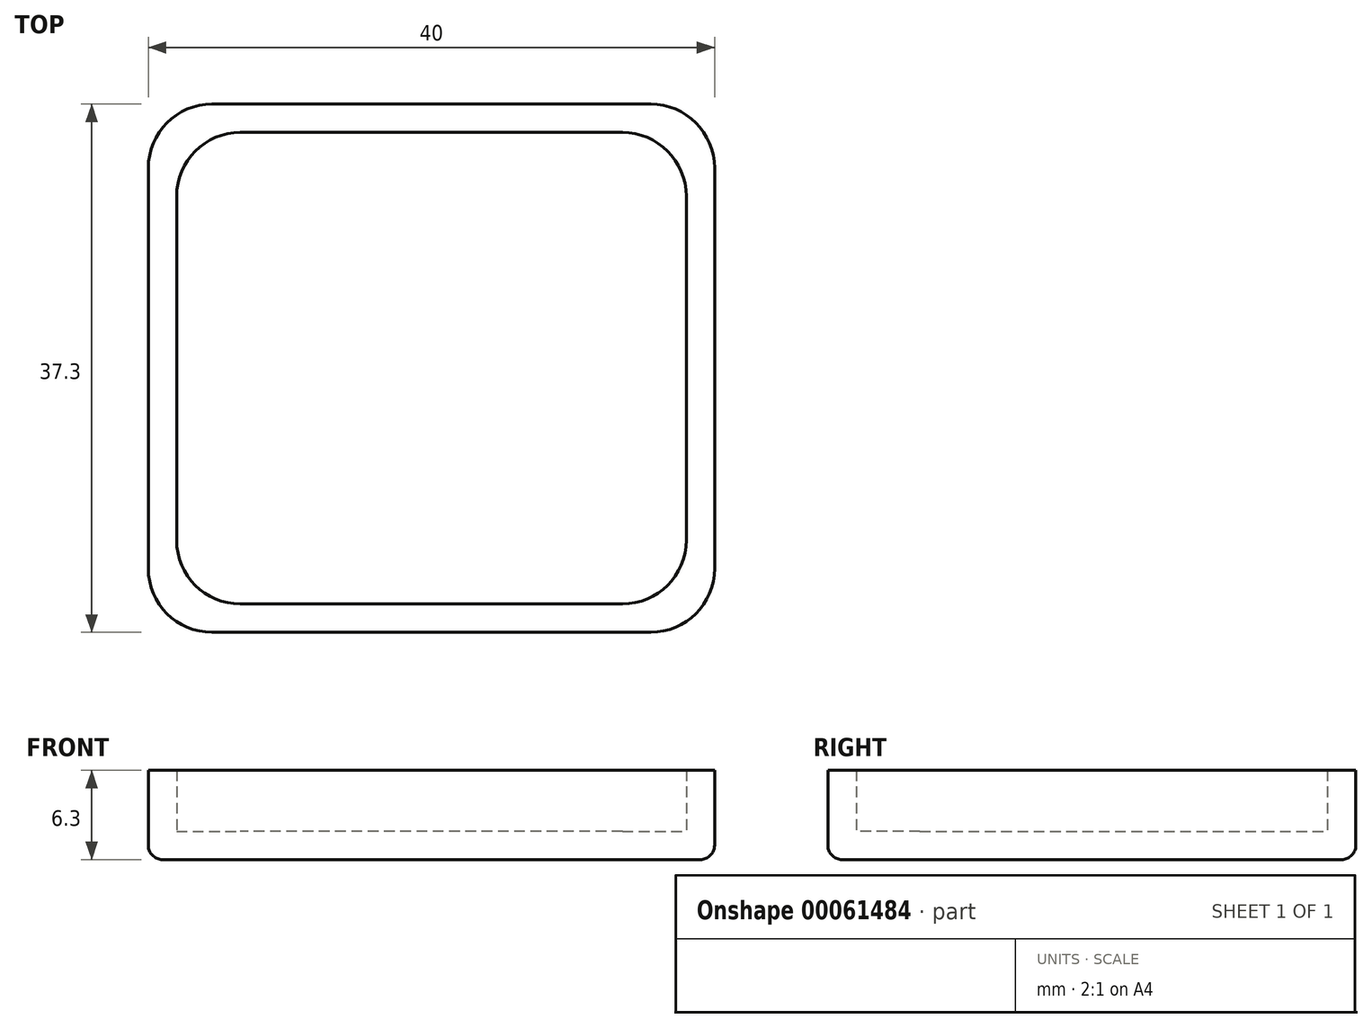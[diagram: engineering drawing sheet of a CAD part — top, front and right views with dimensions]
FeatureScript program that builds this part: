
annotation { "Feature Type Name" : "Feature", "Feature Type Description" : "" }
export const myFeature = defineFeature(function(context is Context, id is Id, definition is map)
    precondition{}
    {
        {
            var Q0;
            Q0=qCreatedBy(makeId("Top.planeOp"),FACE);
            var sketch = newSketch(context, id + "F0", { "sketchPlane" : qUnion([Q0])});
            skLineSegment(sketch, "E0.rect.bottom", {"start": v(18, -16.65) * mm, "end": v(-18, -16.65) * mm});
            skLineSegment(sketch, "E0.rect.top", {"start": v(18, 16.65) * mm, "end": v(-18, 16.65) * mm});
            skLineSegment(sketch, "E0.rect.left", {"start": v(18, -16.65) * mm, "end": v(18, 16.65) * mm});
            skLineSegment(sketch, "E0.rect.right", {"start": v(-18, -16.65) * mm, "end": v(-18, 16.65) * mm});
            skPoint(sketch, "E0.rect.middle", {"position": v(0, 0) * mm});
            skLineSegment(sketch, "E1.0", {"start": v(20, 18.65) * mm, "end": v(-20, 18.65) * mm});
            skLineSegment(sketch, "E1.1", {"start": v(20, -18.65) * mm, "end": v(20, 18.65) * mm});
            skLineSegment(sketch, "E1.2", {"start": v(20, -18.65) * mm, "end": v(-20, -18.65) * mm});
            skLineSegment(sketch, "E1.3", {"start": v(-20, -18.65) * mm, "end": v(-20, 18.65) * mm});
            skSolve(sketch);
        }
        {
            var Q0;
            Q0=makeQuery(id+"F0.imprint","IMPRINT",FACE,{"disambiguationData":[TD([[makeQuery(id+"F0.imprint","IMPRINT",EDGE,{"derivedFrom":sQuery(id+"F0.wireOp",EDGE,"E0.rect.bottom")}),1.0]])]});
            extrude(context, id + "F1", {"entities" : qUnion([Q0]), "depth" : 6.3 * mm});
        }
        {
            var Q0;
            Q0=makeQuery(id+"F0.imprint","IMPRINT",FACE,{"disambiguationData":[TD([[makeQuery(id+"F0.imprint","IMPRINT",EDGE,{"derivedFrom":sQuery(id+"F0.wireOp",EDGE,"E0.rect.bottom")}),-1.0]])]});
            extrude(context, id + "F2", {"entities" : qUnion([Q0]), "operationType" : NewBodyOperationType.ADD, "depth" : 2 * mm});
        }
        {
            var Q0;
            Q0=makeQuery(id+"F1.opExtrude","SWEPT_EDGE",EDGE,{"disambiguationData":[OSD([sQuery(id+"F0.wireOp",EDGE,"E0.rect.top"),sQuery(id+"F0.wireOp",EDGE,"E0.rect.right")])]});
            var Q1;
            Q1=makeQuery(id+"F1.opExtrude","SWEPT_EDGE",EDGE,{"disambiguationData":[OSD([sQuery(id+"F0.wireOp",EDGE,"E0.rect.top"),sQuery(id+"F0.wireOp",EDGE,"E0.rect.left")])]});
            var Q2;
            Q2=makeQuery(id+"F1.opExtrude","SWEPT_EDGE",EDGE,{"disambiguationData":[OSD([sQuery(id+"F0.wireOp",EDGE,"E0.rect.bottom"),sQuery(id+"F0.wireOp",EDGE,"E0.rect.left")])]});
            var Q3;
            Q3=makeQuery(id+"F1.opExtrude","SWEPT_EDGE",EDGE,{"disambiguationData":[OSD([sQuery(id+"F0.wireOp",EDGE,"E0.rect.bottom"),sQuery(id+"F0.wireOp",EDGE,"E0.rect.right")])]});
            var Q4;
            Q4=makeQuery(id+"F1.opExtrude","SWEPT_EDGE",EDGE,{"disambiguationData":[OSD([sQuery(id+"F0.wireOp",EDGE,"E1.2"),sQuery(id+"F0.wireOp",EDGE,"E1.3")])]});
            var Q5;
            Q5=makeQuery(id+"F1.opExtrude","SWEPT_EDGE",EDGE,{"disambiguationData":[OSD([sQuery(id+"F0.wireOp",EDGE,"E1.1"),sQuery(id+"F0.wireOp",EDGE,"E1.2")])]});
            var Q6;
            Q6=makeQuery(id+"F1.opExtrude","SWEPT_EDGE",EDGE,{"disambiguationData":[OSD([sQuery(id+"F0.wireOp",EDGE,"E1.0"),sQuery(id+"F0.wireOp",EDGE,"E1.1")])]});
            var Q7;
            Q7=makeQuery(id+"F1.opExtrude","SWEPT_EDGE",EDGE,{"disambiguationData":[OSD([sQuery(id+"F0.wireOp",EDGE,"E1.0"),sQuery(id+"F0.wireOp",EDGE,"E1.3")])]});
            fillet(context, id + "F3", {"entities" : qUnion([Q0, Q1, Q2, Q3, Q4, Q5, Q6, Q7]), "radius" : 4.5 * mm, "tangentPropagation" : true, "allowEdgeOverflow" : false});
        }
        {
            var Q0;
            Q0=makeQuery(id+"F1.opExtrude","CAP_EDGE",EDGE,{"disambiguationData":[OSD([sQuery(id+"F0.wireOp",EDGE,"E1.2")])],"isStart":true});
            fillet(context, id + "F4", {"entities" : qUnion([Q0]), "radius" : 1 * mm, "tangentPropagation" : true, "allowEdgeOverflow" : false});
        }
    });
